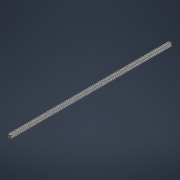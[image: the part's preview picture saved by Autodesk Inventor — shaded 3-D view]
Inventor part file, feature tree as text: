
AUTODESK INVENTOR PART (.ipt)
format: ipt  version: 2021 (Build 250183000, 183)  size: 345,088 bytes
history: native  units: mm
features: extrude x1, pattern_circular x1, chamfer x1, fillet x1, sketch x1, other x1
ambient origin geometry x8: Origin, YZ Plane, XZ Plane, XY Plane, X Axis, Y Axis, Z Axis, Center Point
bodies: Solid1 (feature_tree)
feature tree (6):
  extrude  "Extrusion1"  TaperAngle=135.0deg  [1 undecoded]
  pattern_circular  "Circular Pattern1"  Count=2  [1 undecoded]
  chamfer  "Chamfer1"  Distance=1000.0mm
  fillet  "Fillet1"  Radius=40.0mm
  sketch  "Sketch1"  dims[d0=1.5mm d6=6.3mm d9=4.6mm d18=135.0deg d22=20.0mm d24=1000.0mm d25=0.0mm d26=40.0mm d27=360.0deg d34=11.0mm d35=6.79mm d36=1.8mm d37=1.185mm d38=2.0mm d39=45.0deg d40=1.5mm]
  other  "Image1"
note: 2 required parameter values undecoded (feature->parameter linkage not recoverable at this tier; creation-order binding heuristic only, values carry confidence <= 0.55)
